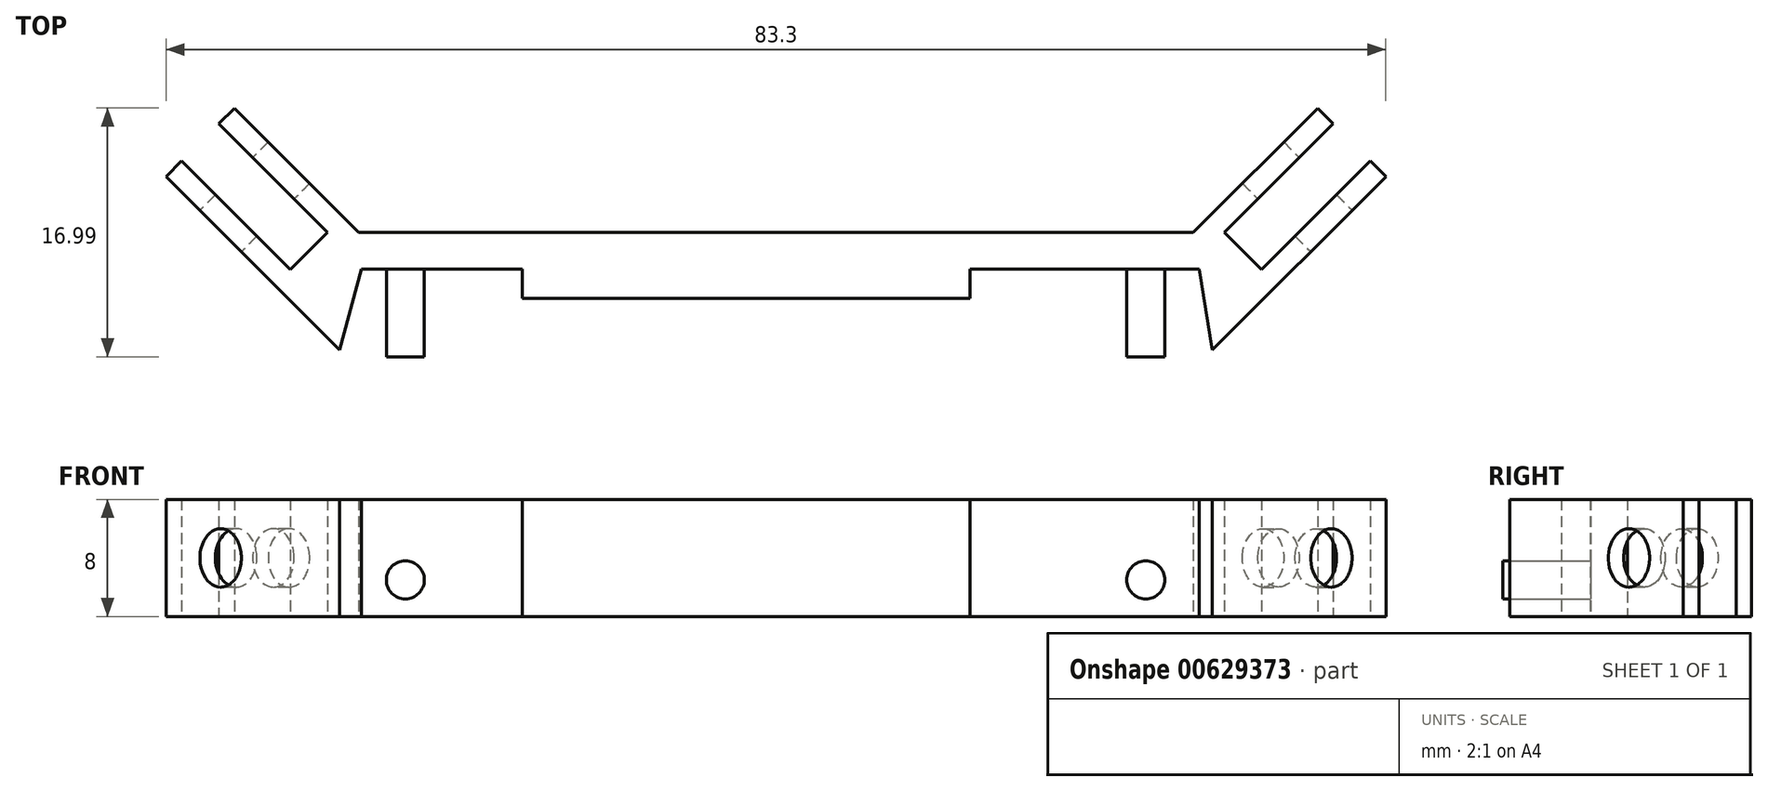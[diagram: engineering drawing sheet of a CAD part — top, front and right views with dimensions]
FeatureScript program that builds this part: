
annotation { "Feature Type Name" : "Feature", "Feature Type Description" : "" }
export const myFeature = defineFeature(function(context is Context, id is Id, definition is map)
    precondition{}
    {
        {
            var Q0;
            Q0=qCreatedBy(makeId("Top.planeOp"),FACE);
            var sketch = newSketch(context, id + "F0", { "sketchPlane" : qUnion([Q0])});
            skLineSegment(sketch, "E0.bottom", {"start": v(-28.5, -30) * mm, "end": v(28.5, -30) * mm});
            skPoint(sketch, "E0.middle", {"position": v(0, 0) * mm});
            skLineSegment(sketch, "E1", {"start": v(30.62, -30) * mm, "end": v(38.05, -22.58) * mm});
            skLineSegment(sketch, "E2.0", {"start": v(33.17, -32.55) * mm, "end": v(40.6, -25.12) * mm});
            skLineSegment(sketch, "E3.0", {"start": v(28.5, -30) * mm, "end": v(36.99, -21.51) * mm});
            skLineSegment(sketch, "E4", {"start": v(30.62, -30) * mm, "end": v(33.17, -32.55) * mm});
            skLineSegment(sketch, "E5.0", {"start": v(29.8, -38.04) * mm, "end": v(41.65, -26.18) * mm});
            skLineSegment(sketch, "E6", {"start": v(36.99, -21.51) * mm, "end": v(38.05, -22.58) * mm});
            skLineSegment(sketch, "E7.0", {"start": v(-28.31, -32.5) * mm, "end": v(28.91, -32.5) * mm});
            skLineSegment(sketch, "E8.trimOffspring", {"start": v(40.6, -25.12) * mm, "end": v(41.65, -26.18) * mm});
            skLineSegment(sketch, "E9.MirrorCS", {"start": v(-29.8, -38.04) * mm, "end": v(-41.65, -26.18) * mm});
            skLineSegment(sketch, "E10.MirrorCS", {"start": v(-40.6, -25.12) * mm, "end": v(-41.65, -26.18) * mm});
            skLineSegment(sketch, "E11.MirrorCS", {"start": v(-33.17, -32.55) * mm, "end": v(-40.6, -25.12) * mm});
            skLineSegment(sketch, "E12.MirrorCS", {"start": v(-30.62, -30) * mm, "end": v(-33.17, -32.55) * mm});
            skLineSegment(sketch, "E13.MirrorCS", {"start": v(-30.62, -30) * mm, "end": v(-38.05, -22.58) * mm});
            skLineSegment(sketch, "E14.MirrorCS", {"start": v(-36.99, -21.51) * mm, "end": v(-38.05, -22.58) * mm});
            skLineSegment(sketch, "E15.MirrorCS", {"start": v(-28.5, -30) * mm, "end": v(-36.99, -21.51) * mm});
            skPoint(sketch, "E16.orphan", {"position": v(-24.26, -32.5) * mm});
            skLineSegment(sketch, "E17", {"start": v(-29.8, -38.04) * mm, "end": v(-28.31, -32.5) * mm});
            skLineSegment(sketch, "E18", {"start": v(29.8, -38.04) * mm, "end": v(28.91, -32.5) * mm});
            skSolve(sketch);
        }
        {
            var Q0;
            Q0=makeQuery(id+"F0.imprint","IMPRINT",FACE,{"disambiguationData":[TD([[makeQuery(id+"F0.imprint","IMPRINT",EDGE,{"derivedFrom":sQuery(id+"F0.wireOp",EDGE,"E0.bottom")}),-1.0]])]});
            extrude(context, id + "F1", {"entities" : qUnion([Q0]), "depth" : 8 * mm, "offsetDistance" : 25 * mm});
        }
        {
            var Q0;
            Q0=makeQuery(id+"F1.opExtrude","SWEPT_FACE",FACE,{"disambiguationData":[OSD([sQuery(id+"F0.wireOp",EDGE,"E5.0")])]});
            var sketch = newSketch(context, id + "F2", { "sketchPlane" : qUnion([Q0])});
            skLineSegment(sketch, "E19.0", {"start": v(5.67, 8) * mm, "end": v(5.67, 6) * mm});
            skLineSegment(sketch, "E20.0", {"start": v(-10.83, -5) * mm, "end": v(-10.83, -5) * mm});
            skLineSegment(sketch, "E20.1", {"start": v(-10.83, 13) * mm, "end": v(-10.83, -5) * mm});
            skLineSegment(sketch, "E20.2", {"start": v(-10.83, 13) * mm, "end": v(-10.83, 13) * mm});
            skLineSegment(sketch, "E20.3", {"start": v(-10.83, 13) * mm, "end": v(-10.83, -5) * mm});
            skCircle(sketch, "E21", {"center": v(5.67, 4) * mm, "radius": 2 * mm});
            skLineSegment(sketch, "E22.trimOffspring", {"start": v(5.67, 2) * mm, "end": v(5.67, 0) * mm});
            skSolve(sketch);
        }
        {
            var Q0;
            {var subQ0=sQuery(id+"F2.wireOp",EDGE,"E21");var subQ1=makeQuery(id+"F2.imprint","INTERSECT",VERTEX,{"derivedFrom":[sQuery(id+"F2.wireOp",EDGE,"E19.0"),subQ0]});Q0=makeQuery(id+"F2.imprint","IMPRINT",FACE,{"disambiguationData":[TD([[makeQuery(id+"F2.imprint","IMPRINT",EDGE,{"disambiguationData":[TD([[subQ1,-1.0]])],"derivedFrom":subQ0}),1.0]])]});}
            extrude(context, id + "F3", {"entities" : qUnion([Q0]), "operationType" : NewBodyOperationType.REMOVE, "oppositeDirection" : true, "depth" : 10 * mm, "offsetDistance" : 25 * mm});
        }
        {
            var Q0;
            Q0=makeQuery(id+"F1.opExtrude","SWEPT_FACE",FACE,{"disambiguationData":[OSD([sQuery(id+"F0.wireOp",EDGE,"E9.MirrorCS")])]});
            var sketch = newSketch(context, id + "F4", { "sketchPlane" : qUnion([Q0])});
            skLineSegment(sketch, "E23.0", {"start": v(-5.67, 8) * mm, "end": v(-5.67, 6) * mm});
            skCircle(sketch, "E24", {"center": v(-5.67, 4) * mm, "radius": 2 * mm});
            skLineSegment(sketch, "E25.trimOffspring", {"start": v(-5.67, 2) * mm, "end": v(-5.67, 0) * mm});
            skSolve(sketch);
        }
        {
            var Q0;
            {var subQ0=sQuery(id+"F4.wireOp",EDGE,"E24");var subQ1=makeQuery(id+"F4.imprint","INTERSECT",VERTEX,{"derivedFrom":[sQuery(id+"F4.wireOp",EDGE,"E23.0"),subQ0]});Q0=makeQuery(id+"F4.imprint","IMPRINT",FACE,{"disambiguationData":[TD([[makeQuery(id+"F4.imprint","IMPRINT",EDGE,{"disambiguationData":[TD([[subQ1,-1.0]])],"derivedFrom":subQ0}),1.0]])]});}
            extrude(context, id + "F5", {"entities" : qUnion([Q0]), "operationType" : NewBodyOperationType.REMOVE, "oppositeDirection" : true, "depth" : 9.9 * mm, "offsetDistance" : 25 * mm});
        }
        {
            var Q0;
            Q0=makeQuery(id+"F1.opExtrude","SWEPT_FACE",FACE,{"disambiguationData":[OSD([sQuery(id+"F0.wireOp",EDGE,"E7.0")])]});
            var sketch = newSketch(context, id + "F6", { "sketchPlane" : qUnion([Q0])});
            skLineSegment(sketch, "E26.0", {"start": v(-33.31, -5) * mm, "end": v(-33.31, -5) * mm});
            skLineSegment(sketch, "E26.1", {"start": v(-33.31, 13) * mm, "end": v(-33.31, -5) * mm});
            skLineSegment(sketch, "E26.2", {"start": v(-33.31, 13) * mm, "end": v(-33.31, 13) * mm});
            skLineSegment(sketch, "E26.3", {"start": v(-33.31, 13) * mm, "end": v(-33.31, -5) * mm});
            skCircle(sketch, "E27", {"center": v(-25.31, 2.5) * mm, "radius": 1.3 * mm});
            skCircle(sketch, "E28", {"center": v(25.26, 2.5) * mm, "radius": 1.3 * mm});
            skLineSegment(sketch, "E29.0", {"start": v(-17.31, 8) * mm, "end": v(-17.31, 0) * mm});
            skLineSegment(sketch, "E30.0", {"start": v(13.26, 8) * mm, "end": v(13.26, 0) * mm});
            skSolve(sketch);
        }
        {
            var Q0;
            {var subQ0=sQuery(id+"F6.wireOp",EDGE,"E29.0");Q0=makeQuery(id+"F6.imprint","IMPRINT",FACE,{"disambiguationData":[TD([[makeQuery(id+"F6.imprint","IMPRINT",EDGE,{"derivedFrom":subQ0}),1.0]])]});}
            extrude(context, id + "F7", {"entities" : qUnion([Q0]), "operationType" : NewBodyOperationType.ADD, "depth" : 2 * mm, "offsetDistance" : 25 * mm});
        }
        {
            var Q0;
            Q0 = qSketchRegion(id + "F6", true);
            extrude(context, id + "F8", {"entities" : qUnion([Q0]), "operationType" : NewBodyOperationType.ADD, "depth" : 6 * mm, "offsetDistance" : 25 * mm});
        }
    });
